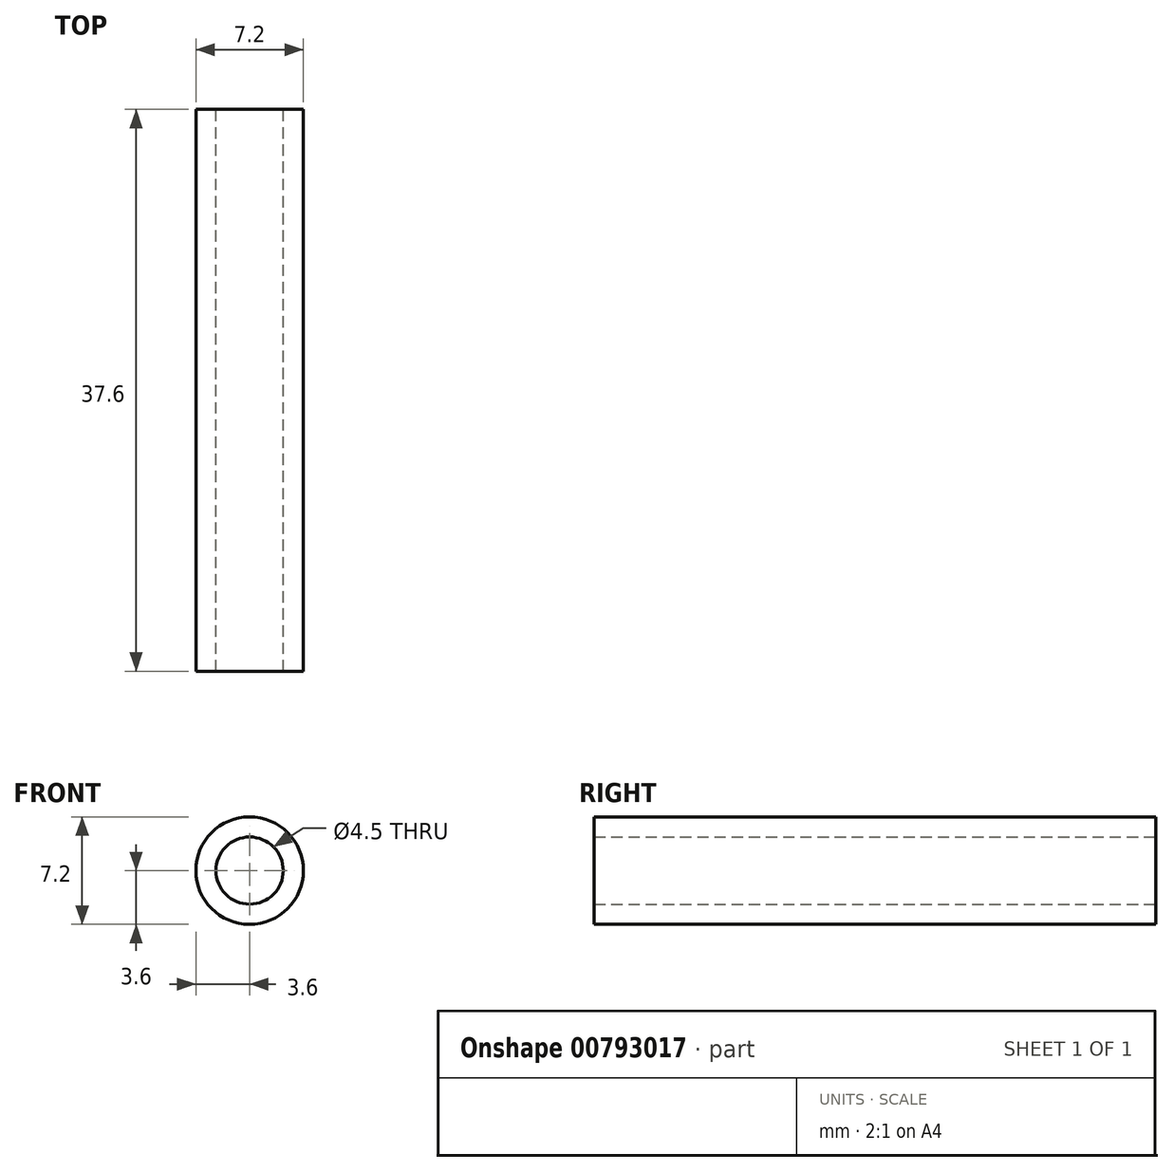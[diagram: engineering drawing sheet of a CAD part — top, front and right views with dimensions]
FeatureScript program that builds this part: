
annotation { "Feature Type Name" : "Feature", "Feature Type Description" : "" }
export const myFeature = defineFeature(function(context is Context, id is Id, definition is map)
    precondition{}
    {
        {
            var Q0;
            Q0=qCreatedBy(makeId("Front.planeOp"),FACE);
            var sketch = newSketch(context, id + "F0", { "sketchPlane" : qUnion([Q0])});
            skCircle(sketch, "E0", {"center": v(0, 0) * mm, "radius": 3.6 * mm});
            skCircle(sketch, "E1", {"center": v(0, 0) * mm, "radius": 2.25 * mm});
            skSolve(sketch);
        }
        {
            var Q0;
            Q0 = qSketchRegion(id + "F0", true);
            extrude(context, id + "F1", {"entities" : qUnion([Q0]), "depth" : 37.6 * mm, "offsetDistance" : 25 * mm});
        }
    });
